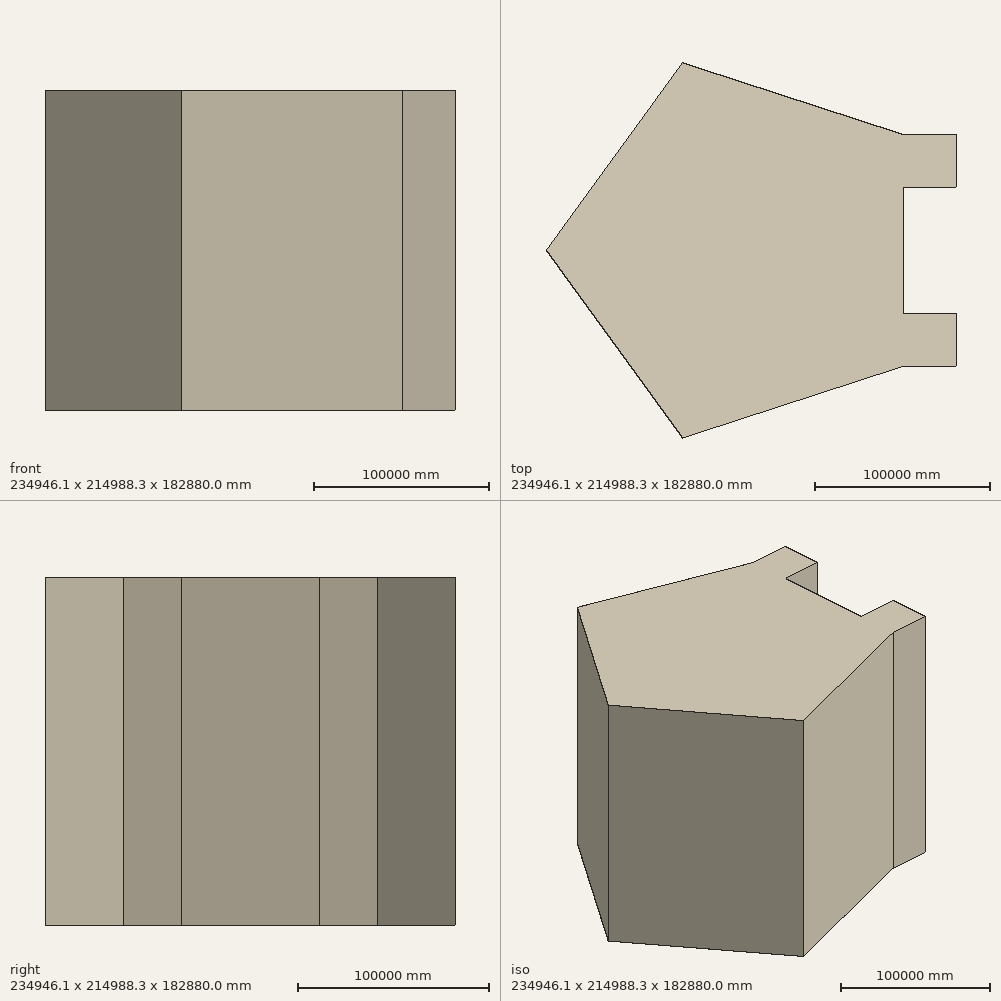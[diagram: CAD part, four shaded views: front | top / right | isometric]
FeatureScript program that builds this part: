
annotation { "Feature Type Name" : "Feature", "Feature Type Description" : "" }
export const myFeature = defineFeature(function(context is Context, id is Id, definition is map)
    precondition{}
    {
        {
            var Q0;
            Q0=qCreatedBy(makeId("Top.planeOp"),FACE);
            var sketch = newSketch(context, id + "F0", { "sketchPlane" : qUnion([Q0])});
            skLineSegment(sketch, "E0", {"start": v(0, 0) * mm, "end": v(91440, 0) * mm});
            skLineSegment(sketch, "E1", {"start": v(91440, 0) * mm, "end": v(0, 0) * mm});
            skLineSegment(sketch, "E2", {"start": v(0, 0) * mm, "end": v(-91440, 0) * mm});
            skCircle(sketch, "E3.cCircle", {"center": v(0, 0) * mm, "radius": 91440 * mm, "construction": true});
            skLineSegment(sketch, "E3.0", {"start": v(91440, 66435.05) * mm, "end": v(91440, -66435.05) * mm});
            skLineSegment(sketch, "E3.1", {"start": v(91440, -66435.05) * mm, "end": v(-34926.97, -107494.17) * mm});
            skLineSegment(sketch, "E3.2", {"start": v(-34926.97, -107494.17) * mm, "end": v(-113026.06, 0) * mm});
            skLineSegment(sketch, "E3.3", {"start": v(-113026.06, 0) * mm, "end": v(-34926.97, 107494.17) * mm});
            skLineSegment(sketch, "E3.4", {"start": v(-34926.97, 107494.17) * mm, "end": v(91440, 66435.05) * mm});
            skPoint(sketch, "E3.0.midPoint", {"position": v(91440, 0) * mm});
            skLineSegment(sketch, "E4.bottom", {"start": v(91440, 66435.05) * mm, "end": v(121920, 66435.05) * mm});
            skLineSegment(sketch, "E4.top", {"start": v(91440, 35955.05) * mm, "end": v(121920, 35955.05) * mm});
            skLineSegment(sketch, "E4.left", {"start": v(91440, 66435.05) * mm, "end": v(91440, 35955.05) * mm});
            skLineSegment(sketch, "E4.right", {"start": v(121920, 66435.05) * mm, "end": v(121920, 35955.05) * mm});
            skLineSegment(sketch, "E5.bottom", {"start": v(91440, -66435.05) * mm, "end": v(121920, -66435.05) * mm});
            skLineSegment(sketch, "E5.top", {"start": v(91440, -35955.05) * mm, "end": v(121920, -35955.05) * mm});
            skLineSegment(sketch, "E5.left", {"start": v(91440, -66435.05) * mm, "end": v(91440, -35955.05) * mm});
            skLineSegment(sketch, "E5.right", {"start": v(121920, -66435.05) * mm, "end": v(121920, -35955.05) * mm});
            skSolve(sketch);
        }
        {
            var Q0;
            Q0=makeQuery(id+"F0.imprint","IMPRINT",FACE,{"disambiguationData":[TD([[makeQuery(id+"F0.imprint","IMPRINT",EDGE,{"derivedFrom":sQuery(id+"F0.wireOp",EDGE,"E3.1")}),-1.0]])]});
            var Q1;
            Q1=makeQuery(id+"F0.imprint","IMPRINT",FACE,{"disambiguationData":[TD([[makeQuery(id+"F0.imprint","IMPRINT",EDGE,{"derivedFrom":sQuery(id+"F0.wireOp",EDGE,"E4.bottom")}),-1.0]])]});
            var Q2;
            Q2=makeQuery(id+"F0.imprint","IMPRINT",FACE,{"disambiguationData":[TD([[makeQuery(id+"F0.imprint","IMPRINT",EDGE,{"derivedFrom":sQuery(id+"F0.wireOp",EDGE,"E5.bottom")}),1.0]])]});
            extrude(context, id + "F1", {"entities" : qUnion([Q0, Q1, Q2]), "depth" : 182880 * mm, "offsetDistance" : 30.48 * mm});
        }
    });
